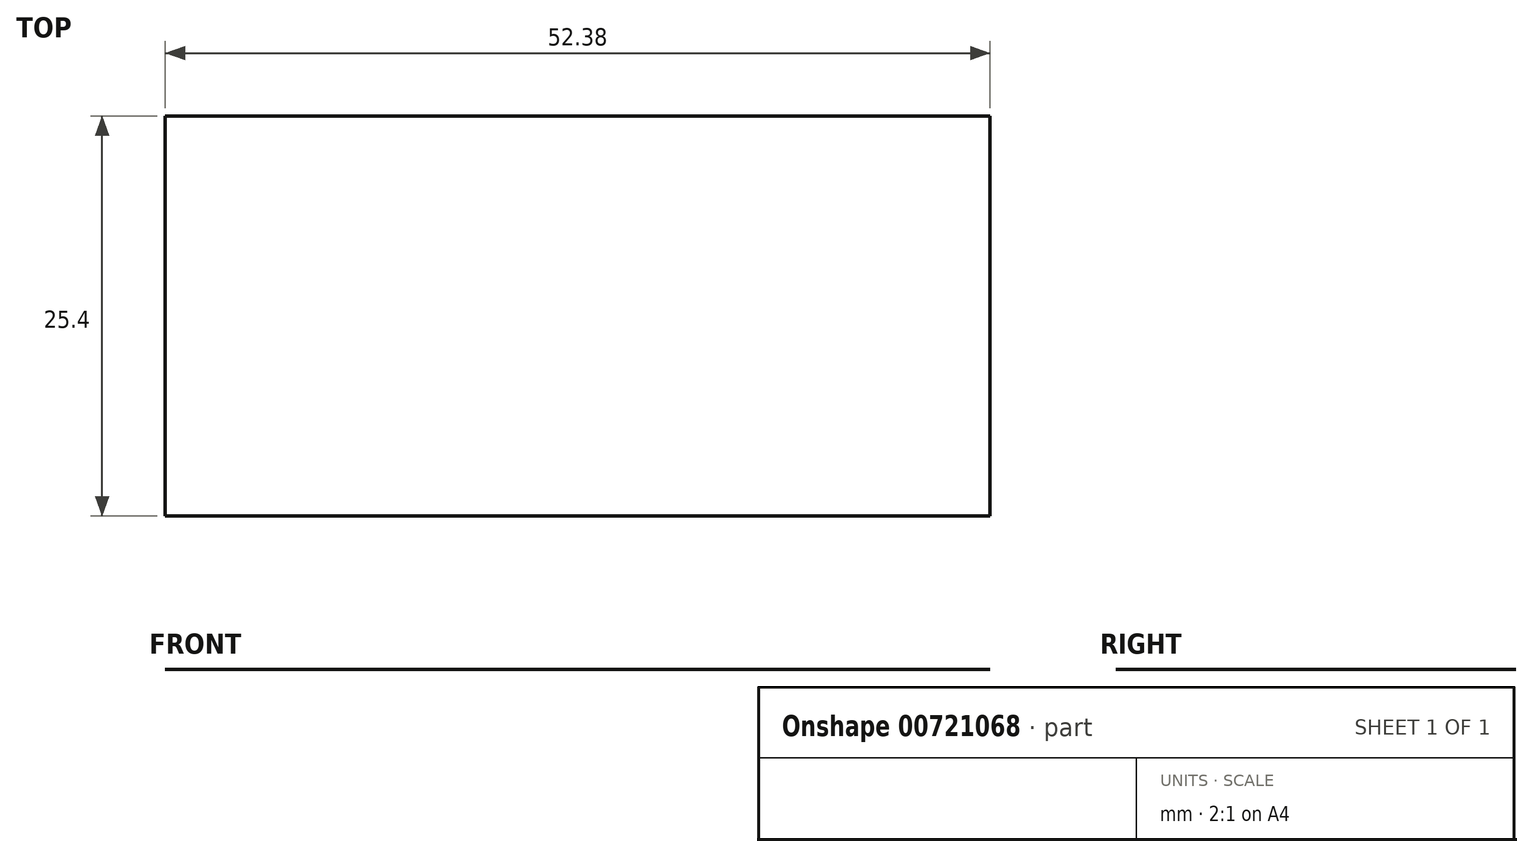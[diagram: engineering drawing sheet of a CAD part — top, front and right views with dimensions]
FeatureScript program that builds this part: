
annotation { "Feature Type Name" : "Feature", "Feature Type Description" : "" }
export const myFeature = defineFeature(function(context is Context, id is Id, definition is map)
    precondition{}
    {
        {
            var Q0;
            Q0=qCreatedBy(makeId("Front.planeOp"),FACE);
            var sketch = newSketch(context, id + "F0", { "sketchPlane" : qUnion([Q0])});
            skLineSegment(sketch, "E0", {"start": v(0, 0) * mm, "end": v(-52.38, 0) * mm});
            skLineSegment(sketch, "E1", {"start": v(0, 0) * mm, "end": v(0, 30.45) * mm});
            skLineSegment(sketch, "E2", {"start": v(0, 30.45) * mm, "end": v(74.9, 30.45) * mm});
            skLineSegment(sketch, "E3", {"start": v(74.9, 30.45) * mm, "end": v(74.9, 0) * mm});
            skLineSegment(sketch, "E4", {"start": v(74.9, 0) * mm, "end": v(110.92, 0) * mm});
            skLineSegment(sketch, "E5", {"start": v(0, 0) * mm, "end": v(74.9, 0) * mm});
            skSolve(sketch);
        }
        {
            var Q0;
            Q0=sQuery(id+"F0.wireOp",EDGE,"E0");
            extrude(context, id + "F1", {"bodyType" : ToolBodyType.SURFACE, "surfaceEntities" : qUnion([Q0]), "endBound" : BoundingType.SYMMETRIC, "depth" : 25.4 * mm, "offsetDistance" : 25.4 * mm});
        }
    });
